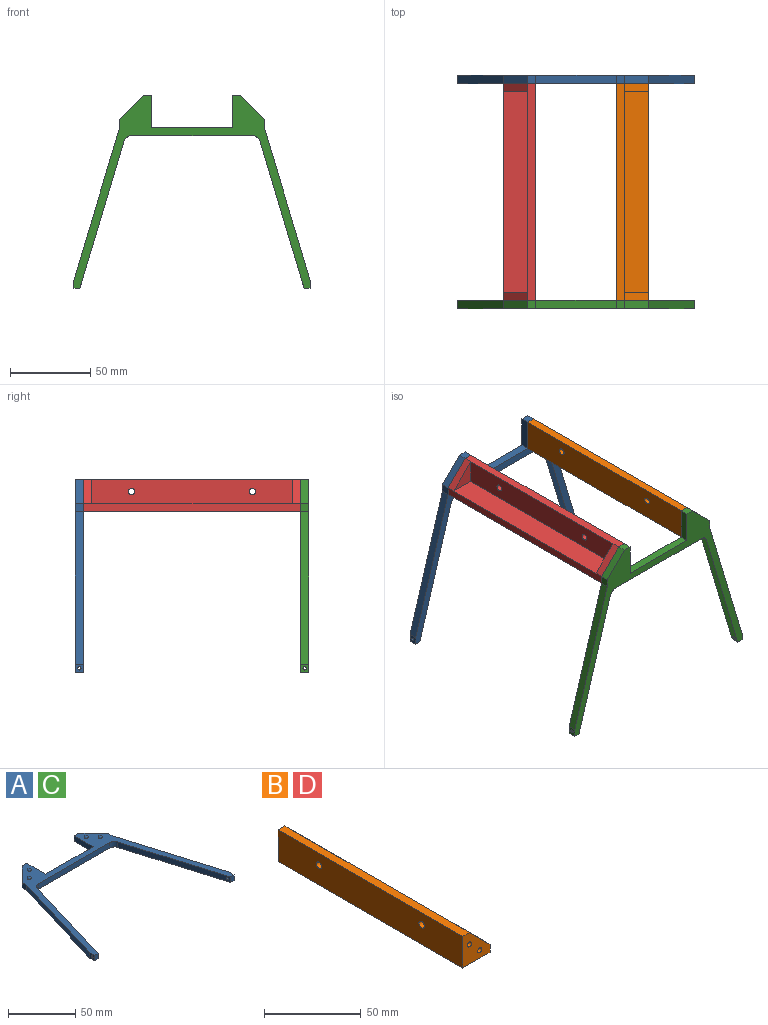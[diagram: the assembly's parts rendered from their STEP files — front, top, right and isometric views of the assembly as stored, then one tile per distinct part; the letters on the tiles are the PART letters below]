
ASSEMBLY  parts=4 mates=3
PART A: 28 faces, bbox 147x120x6.5 mm
  f0: plane 75.12x5mm, normal (0,-1,0), area 375.6mm2, adj f18,f19,f20,f21
  f1: plane 91.44x27.43mm, normal (-0.96,-0.29,0), area 474mm2, adj f2,f18,f19,f20,f23
  f2: plane 5x3.72mm, normal (0,-1,0), area 18.6mm2, adj f1,f3,f18,f19
  f3: plane 5x5mm, normal (1,0,0), area 21.9mm2, adj f2,f4,f18,f19,f23
  f4: plane 95x28.5mm, normal (0.96,0.29,0), area 495.9mm2, adj f3,f5,f18,f19
  f5: plane 5x5mm, normal (1,0,0), area 25mm2, adj f4,f6,f18,f19
  f6: plane 15x15mm, normal (0.71,0.71,0), area 106.1mm2, adj f5,f7,f18,f19
  f7: plane 5x5mm, normal (0,1,0), area 25mm2, adj f6,f8,f18,f19
  f8: plane 20x5mm, normal (-1,0,0), area 100mm2, adj f7,f9,f18,f19
  f9: plane 50x5mm, normal (0,1,0), area 250mm2, adj f8,f10,f18,f19
  f10: plane 20x5mm, normal (1,0,0), area 100mm2, adj f9,f11,f18,f19
  f11: plane 5x5mm, normal (0,1,0), area 25mm2, adj f10,f12,f18,f19
  f12: plane 15x15mm, normal (-0.71,0.71,0), area 106.1mm2, adj f11,f13,f18,f19
  f13: plane 5x5mm, normal (-1,0,0), area 25mm2, adj f12,f14,f18,f19
  f14: plane 95x28.5mm, normal (-0.96,0.29,0), area 495.9mm2, adj f13,f15,f18,f19
  f15: plane 5x5mm, normal (-1,0,0), area 21.9mm2, adj f14,f16,f18,f19,f22
  f16: plane 5x3.72mm, normal (0,-1,0), area 18.6mm2, adj f15,f17,f18,f19
  f17: plane 91.44x27.43mm, normal (0.96,-0.29,0), area 474mm2, adj f16,f18,f19,f21,f22
  f18: plane 147x120mm, normal (0,0,1), area 1993.8mm2, adj f0,f1,f2,f3,f4,f5,f6,f7
  f19: plane 147x120mm, normal (0,0,-1), area 2022mm2, adj f0,f1,f2,f3,f4,f5,f6,f7
  f20: cylinder r=5mm len=5mm, axis (0,0,1), area 32mm2, adj f0,f1,f18,f19
  f21: cylinder r=5mm len=5mm, axis (0,0,1), area 32mm2, adj f0,f17,f18,f19
  f22: cylinder r=1mm len=4.77mm, axis (-1,0,0), area 28.1mm2, adj f15,f17
  f23: cylinder r=1mm len=4.77mm, axis (-1,0,0), area 28.1mm2, adj f1,f3
  f24: sphere r=1.5mm, area 14.1mm2, adj f18
  f25: sphere r=1.5mm, area 14.1mm2, adj f18
  f26: sphere r=1.5mm, area 14.1mm2, adj f18
  f27: sphere r=1.5mm, area 14.1mm2, adj f18
PART B: 18 faces, bbox 20x135x20 mm
  f0: plane 15x15mm, normal (0,-1,0), area 112.5mm2, adj f4,f7,f8
  f1: plane 135x20mm, normal (-1,0,0), area 2674.9mm2, adj f2,f5,f6,f10,f12,f13
  f2: plane 135x20mm, normal (0,0,-1), area 2700mm2, adj f1,f3,f6,f10
  f3: plane 135x5mm, normal (1,0,0), area 675mm2, adj f2,f4,f6,f8,f9,f10
  f4: plane 15x15mm, normal (0.71,0,0.71), area 106.1mm2, adj f0,f3,f5,f6
  f5: plane 135x5mm, normal (0,0,1), area 675mm2, adj f1,f4,f6,f7,f9,f10
  f6: plane 20x20mm, normal (0,1,0), area 273.4mm2, adj f1,f2,f3,f4,f5,f16,f17
  f7: plane 125x15mm, normal (1,0,0), area 1849.9mm2, adj f0,f5,f8,f11,f12,f13
  f8: plane 125x15mm, normal (0,0,1), area 1875mm2, adj f0,f3,f7,f11
  f9: plane 15x15mm, normal (0.71,0,0.71), area 106.1mm2, adj f3,f5,f10,f11
  f10: plane 20x20mm, normal (0,-1,0), area 273.4mm2, adj f1,f2,f3,f5,f9,f14,f15
  f11: plane 15x15mm, normal (0,1,0), area 112.5mm2, adj f7,f8,f9
  f12: cylinder r=2mm len=5mm, axis (1,0,0), area 62.8mm2, adj f1,f7
  f13: cylinder r=2mm len=5mm, axis (1,0,0), area 62.8mm2, adj f1,f7
  f14: sphere r=1.5mm, area 14.1mm2, adj f10
  f15: sphere r=1.5mm, area 14.1mm2, adj f10
  f16: sphere r=1.5mm, area 14.1mm2, adj f6
  f17: sphere r=1.5mm, area 14.1mm2, adj f6
PART C: same geometry as A
PART D: same geometry as B
PLACE A rot(axis=(1,0,0),90deg) t=(-125.71,56.46,-129.3)mm
PLACE B t=(-15.48,51.46,-29.3)mm fixed
PLACE C rot(axis=(0,0.71,0.71),180deg) t=(44.74,-88.54,-129.3)mm
PLACE D rot(axis=(0,0,1),180deg) t=(-65.48,-83.54,-29.3)mm
MATE fastened D.f6 <-> C.f18  axis (0,-1,0) through (-70.48,-83.54,-16.8)mm
MATE fastened A.f18 <-> B.f6  axis (0,-1,0) through (-10.48,51.46,-16.8)mm
MATE fastened D.f10 <-> A.f18  axis (0,1,0) through (-70.48,51.46,-16.8)mm
